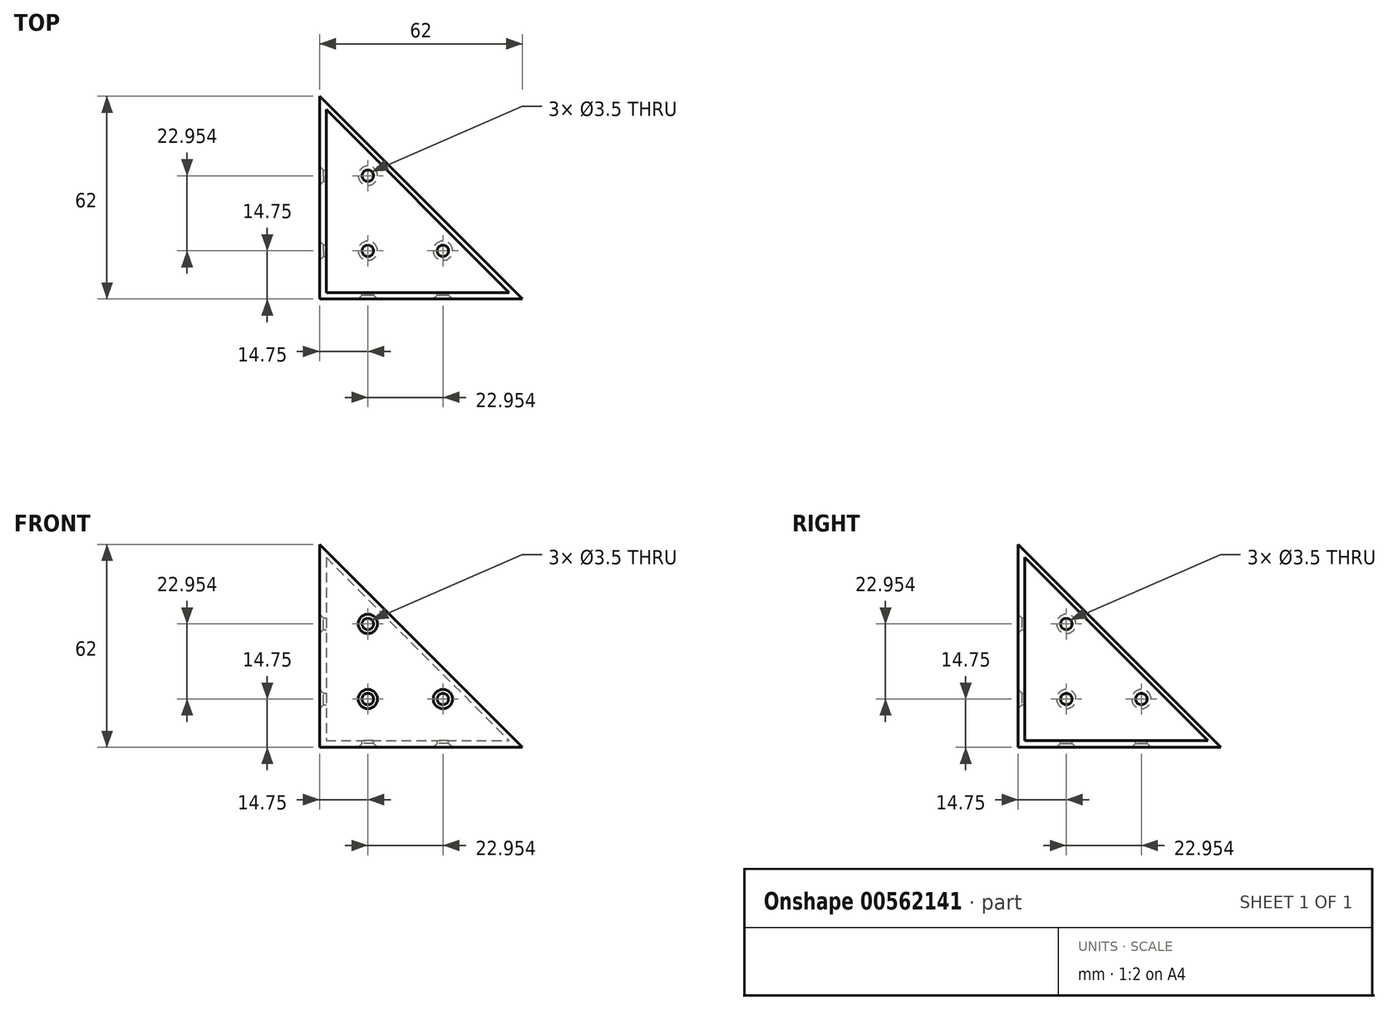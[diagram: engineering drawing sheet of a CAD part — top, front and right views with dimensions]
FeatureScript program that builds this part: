
annotation { "Feature Type Name" : "Feature", "Feature Type Description" : "" }
export const myFeature = defineFeature(function(context is Context, id is Id, definition is map)
    precondition{}
    {
        {
            var Q0;
            Q0=qCreatedBy(makeId("Top.planeOp"),FACE);
            var sketch = newSketch(context, id + "F0", { "sketchPlane" : qUnion([Q0])});
            skLineSegment(sketch, "E0", {"start": v(31, 31) * mm, "end": v(0, 0) * mm});
            skLineSegment(sketch, "E1", {"start": v(0, 0) * mm, "end": v(62, 0) * mm});
            skLineSegment(sketch, "E2", {"start": v(62, 0) * mm, "end": v(31, 31) * mm});
            skSolve(sketch);
        }
        {
            var Q0;
            Q0 = qSketchRegion(id + "F0", true);
            extrude(context, id + "F1", {"entities" : qUnion([Q0]), "depth" : 2 * mm, "offsetDistance" : 25 * mm});
        }
        {
            var Q0;
            Q0=makeQuery(id+"F1.opExtrude","CAP_FACE",FACE,{"disambiguationData":[OSD([sQuery(id+"F0.wireOp",EDGE,"E0"),sQuery(id+"F0.wireOp",EDGE,"E1"),sQuery(id+"F0.wireOp",EDGE,"E2")])],"isStart":false});
            var sketch = newSketch(context, id + "F2", { "sketchPlane" : qUnion([Q0])});
            skLineSegment(sketch, "E3", {"start": v(0, 0) * mm, "end": v(62, 0) * mm});
            skLineSegment(sketch, "E4", {"start": v(62, 0) * mm, "end": v(60, 2) * mm});
            skLineSegment(sketch, "E5", {"start": v(60, 2) * mm, "end": v(2, 2) * mm});
            skLineSegment(sketch, "E6", {"start": v(2, 2) * mm, "end": v(0, 0) * mm});
            skSolve(sketch);
        }
        {
            var Q0;
            Q0=makeQuery(id+"F2.imprint","IMPRINT",FACE,{"disambiguationData":[TD([[makeQuery(id+"F2.imprint","IMPRINT",EDGE,{"derivedFrom":sQuery(id+"F2.wireOp",EDGE,"E3")}),1.0]])]});
            extrude(context, id + "F3", {"entities" : qUnion([Q0]), "operationType" : NewBodyOperationType.ADD, "depth" : 60 * mm, "offsetDistance" : 25 * mm});
        }
        {
            var Q0;
            Q0=makeQuery(id+"F3.boolean.opBoolean","MERGE",FACE,{"derivedFrom":[makeQuery(id+"F1.opExtrude","SWEPT_FACE",FACE,{"disambiguationData":[OSD([sQuery(id+"F0.wireOp",EDGE,"E1")])]}),makeQuery(id+"F3.opExtrude","SWEPT_FACE",FACE,{"disambiguationData":[OSD([sQuery(id+"F2.wireOp",EDGE,"E3")])]})]});
            var sketch = newSketch(context, id + "F4", { "sketchPlane" : qUnion([Q0])});
            skLineSegment(sketch, "E7", {"start": v(0, 62) * mm, "end": v(62, 0) * mm});
            skSolve(sketch);
        }
        {
            var Q0;
            Q0=makeQuery(id+"F4.imprint","IMPRINT",FACE,{"disambiguationData":[TD([[makeQuery(id+"F4.imprint","IMPRINT",EDGE,{"derivedFrom":sQuery(id+"F4.wireOp",EDGE,"E7")}),1.0]])]});
            extrude(context, id + "F5", {"entities" : qUnion([Q0]), "operationType" : NewBodyOperationType.REMOVE, "endBound" : BoundingType.THROUGH_ALL, "oppositeDirection" : true, "depth" : 25 * mm, "offsetDistance" : 25 * mm});
        }
        {
            var Q0;
            Q0=makeQuery(id+"F3.opExtrude","SWEPT_FACE",FACE,{"disambiguationData":[OSD([sQuery(id+"F2.wireOp",EDGE,"E5")])]});
            var sketch = newSketch(context, id + "F6", { "sketchPlane" : qUnion([Q0])});
            skCircle(sketch, "E8", {"center": v(-14.75, 14.75) * mm, "radius": 1.75 * mm});
            skCircle(sketch, "E9", {"center": v(-14.75, 37.7) * mm, "radius": 1.75 * mm});
            skCircle(sketch, "E10", {"center": v(-37.7, 14.75) * mm, "radius": 1.75 * mm});
            skSolve(sketch);
        }
        {
            var Q0;
            Q0 = qSketchRegion(id + "F6", true);
            extrude(context, id + "F7", {"entities" : qUnion([Q0]), "operationType" : NewBodyOperationType.REMOVE, "endBound" : BoundingType.THROUGH_ALL, "oppositeDirection" : true, "depth" : 25 * mm, "offsetDistance" : 25 * mm});
        }
        {
            var Q0;
            Q0=makeQuery(id+"F1.opExtrude","SWEPT_BODY",BODY,{"disambiguationData":[OSD([sQuery(id+"F0.wireOp",EDGE,"E0"),sQuery(id+"F0.wireOp",EDGE,"E1"),sQuery(id+"F0.wireOp",EDGE,"E2")])]});
            var Q1;
            Q1=makeQuery(id+"F3.boolean.opBoolean","MERGE",FACE,{"derivedFrom":[makeQuery(id+"F1.opExtrude","SWEPT_FACE",FACE,{"disambiguationData":[OSD([sQuery(id+"F0.wireOp",EDGE,"E0")])]}),makeQuery(id+"F3.opExtrude","SWEPT_FACE",FACE,{"disambiguationData":[OSD([sQuery(id+"F2.wireOp",EDGE,"E6")])]})]});
            mirror(context, id + "F8", {"operationType" : NewBodyOperationType.ADD, "entities" : qUnion([Q0]), "mirrorPlane" : qUnion([Q1])});
        }
        {
            var Q0;
            {var subQ0=makeQuery(id+"F1.opExtrude","CAP_FACE",FACE,{"disambiguationData":[OSD([sQuery(id+"F0.wireOp",EDGE,"E0"),sQuery(id+"F0.wireOp",EDGE,"E1"),sQuery(id+"F0.wireOp",EDGE,"E2")])],"isStart":false});Q0=makeQuery(id+"F8.boolean.opBoolean","MERGE",FACE,{"derivedFrom":[subQ0,makeQuery(id+"F8.opPattern","COPY",FACE,{"derivedFrom":subQ0,"instanceName":"1"})]});}
            var sketch = newSketch(context, id + "F9", { "sketchPlane" : qUnion([Q0])});
            skCircle(sketch, "E11", {"center": v(14.75, 14.75) * mm, "radius": 1.75 * mm});
            skCircle(sketch, "E12", {"center": v(37.7, 14.75) * mm, "radius": 1.75 * mm});
            skCircle(sketch, "E13", {"center": v(14.75, 37.7) * mm, "radius": 1.75 * mm});
            skSolve(sketch);
        }
        {
            var Q0;
            Q0 = qSketchRegion(id + "F9", true);
            extrude(context, id + "F10", {"entities" : qUnion([Q0]), "operationType" : NewBodyOperationType.REMOVE, "endBound" : BoundingType.THROUGH_ALL, "oppositeDirection" : true, "depth" : 25 * mm, "offsetDistance" : 25 * mm});
        }
        {
            var Q0;
            {var subQ0=sQuery(id+"F0.wireOp",EDGE,"E2");var subQ1=sQuery(id+"F0.wireOp",EDGE,"E1");Q0=makeQuery(id+"F5.boolean.opBoolean","MERGE",VERTEX,{"derivedFrom":[makeQuery(id+"F1.opExtrude","CAP_VERTEX",VERTEX,{"disambiguationData":[OSD([subQ1,subQ0])],"isStart":true}),makeQuery(id+"F5.opExtrude","CAP_VERTEX",VERTEX,{"disambiguationData":[OSD([subQ1,subQ0,sQuery(id+"F2.wireOp",EDGE,"E3"),sQuery(id+"F2.wireOp",EDGE,"E4"),sQuery(id+"F4.wireOp",EDGE,"E7")])],"isStart":true})]});}
            var Q1;
            {var subQ0=sQuery(id+"F0.wireOp",EDGE,"E2");var subQ1=sQuery(id+"F0.wireOp",EDGE,"E1");Q1=makeQuery(id+"F8.opPattern","COPY",VERTEX,{"derivedFrom":makeQuery(id+"F5.boolean.opBoolean","MERGE",VERTEX,{"derivedFrom":[makeQuery(id+"F1.opExtrude","CAP_VERTEX",VERTEX,{"disambiguationData":[OSD([subQ1,subQ0])],"isStart":true}),makeQuery(id+"F5.opExtrude","CAP_VERTEX",VERTEX,{"disambiguationData":[OSD([subQ1,subQ0,sQuery(id+"F2.wireOp",EDGE,"E3"),sQuery(id+"F2.wireOp",EDGE,"E4"),sQuery(id+"F4.wireOp",EDGE,"E7")])],"isStart":true})]}),"instanceName":"1"});}
            var Q2;
            {var subQ0=sQuery(id+"F2.wireOp",EDGE,"E6");var subQ1=sQuery(id+"F2.wireOp",EDGE,"E3");var subQ2=makeQuery(id+"F5.boolean.opBoolean","MERGE",VERTEX,{"derivedFrom":[makeQuery(id+"F3.opExtrude","CAP_VERTEX",VERTEX,{"disambiguationData":[OSD([subQ1,subQ0])],"isStart":false}),makeQuery(id+"F5.opExtrude","CAP_VERTEX",VERTEX,{"disambiguationData":[OSD([sQuery(id+"F0.wireOp",EDGE,"E0"),sQuery(id+"F0.wireOp",EDGE,"E1"),subQ1,subQ0,sQuery(id+"F4.wireOp",EDGE,"E7")])],"isStart":true})]});Q2=makeQuery(id+"F8.boolean.opBoolean","MERGE",VERTEX,{"derivedFrom":[subQ2,makeQuery(id+"F8.opPattern","COPY",VERTEX,{"derivedFrom":subQ2,"instanceName":"1"})]});}
            cPlane(context, id + "F11", {"entities" : qUnion([Q0, Q1, Q2]), "cplaneType" : CPlaneType.THREE_POINT, "offset" : 25 * mm, "width" : 150 * mm, "height" : 150 * mm});
        }
        {
            var Q0;
            Q0=qCreatedBy(id+"F11.planeOp",FACE);
            var sketch = newSketch(context, id + "F12", { "sketchPlane" : qUnion([Q0])});
            skPoint(sketch, "E14.0", {"position": v(-25.31, 43.84) * mm});
            skPoint(sketch, "E14.1", {"position": v(50.62, 0) * mm});
            skPoint(sketch, "E14.2", {"position": v(-25.31, -43.84) * mm});
            skLineSegment(sketch, "E15", {"start": v(50.62, 0) * mm, "end": v(-25.31, 43.84) * mm});
            skLineSegment(sketch, "E16", {"start": v(-25.31, -43.84) * mm, "end": v(50.62, 0) * mm});
            skLineSegment(sketch, "E17", {"start": v(-25.31, -43.84) * mm, "end": v(-25.31, 43.84) * mm});
            skSolve(sketch);
        }
        {
            var Q0;
            Q0 = qSketchRegion(id + "F12", true);
            extrude(context, id + "F13", {"entities" : qUnion([Q0]), "operationType" : NewBodyOperationType.REMOVE, "endBound" : BoundingType.THROUGH_ALL, "oppositeDirection" : true, "depth" : 25 * mm, "offsetDistance" : 25 * mm});
        }
        {
            var Q0;
            {var subQ0=makeQuery(id+"F1.opExtrude","CAP_FACE",FACE,{"disambiguationData":[OSD([sQuery(id+"F0.wireOp",EDGE,"E0"),sQuery(id+"F0.wireOp",EDGE,"E1"),sQuery(id+"F0.wireOp",EDGE,"E2")])],"isStart":true});Q0=makeQuery(id+"F10.boolean.opBoolean","INTERSECT",EDGE,{"derivedFrom":[makeQuery(id+"F8.boolean.opBoolean","MERGE",FACE,{"derivedFrom":[subQ0,makeQuery(id+"F8.opPattern","COPY",FACE,{"derivedFrom":subQ0,"instanceName":"1"})]}),makeQuery(id+"F10.opExtrude","SWEPT_FACE",FACE,{"disambiguationData":[OSD([sQuery(id+"F9.wireOp",EDGE,"E13")])]})]});}
            var Q1;
            {var subQ0=makeQuery(id+"F1.opExtrude","CAP_FACE",FACE,{"disambiguationData":[OSD([sQuery(id+"F0.wireOp",EDGE,"E0"),sQuery(id+"F0.wireOp",EDGE,"E1"),sQuery(id+"F0.wireOp",EDGE,"E2")])],"isStart":true});Q1=makeQuery(id+"F10.boolean.opBoolean","INTERSECT",EDGE,{"derivedFrom":[makeQuery(id+"F8.boolean.opBoolean","MERGE",FACE,{"derivedFrom":[subQ0,makeQuery(id+"F8.opPattern","COPY",FACE,{"derivedFrom":subQ0,"instanceName":"1"})]}),makeQuery(id+"F10.opExtrude","SWEPT_FACE",FACE,{"disambiguationData":[OSD([sQuery(id+"F9.wireOp",EDGE,"E11")])]})]});}
            var Q2;
            {var subQ0=makeQuery(id+"F1.opExtrude","CAP_FACE",FACE,{"disambiguationData":[OSD([sQuery(id+"F0.wireOp",EDGE,"E0"),sQuery(id+"F0.wireOp",EDGE,"E1"),sQuery(id+"F0.wireOp",EDGE,"E2")])],"isStart":true});Q2=makeQuery(id+"F10.boolean.opBoolean","INTERSECT",EDGE,{"derivedFrom":[makeQuery(id+"F8.boolean.opBoolean","MERGE",FACE,{"derivedFrom":[subQ0,makeQuery(id+"F8.opPattern","COPY",FACE,{"derivedFrom":subQ0,"instanceName":"1"})]}),makeQuery(id+"F10.opExtrude","SWEPT_FACE",FACE,{"disambiguationData":[OSD([sQuery(id+"F9.wireOp",EDGE,"E12")])]})]});}
            var Q3;
            Q3=makeQuery(id+"F8.opPattern","COPY",EDGE,{"derivedFrom":makeQuery(id+"F7.boolean.opBoolean","INTERSECT",EDGE,{"derivedFrom":[makeQuery(id+"F3.boolean.opBoolean","MERGE",FACE,{"derivedFrom":[makeQuery(id+"F1.opExtrude","SWEPT_FACE",FACE,{"disambiguationData":[OSD([sQuery(id+"F0.wireOp",EDGE,"E1")])]}),makeQuery(id+"F3.opExtrude","SWEPT_FACE",FACE,{"disambiguationData":[OSD([sQuery(id+"F2.wireOp",EDGE,"E3")])]})]}),makeQuery(id+"F7.opExtrude","SWEPT_FACE",FACE,{"disambiguationData":[OSD([sQuery(id+"F6.wireOp",EDGE,"E8")])]})]}),"instanceName":"1"});
            var Q4;
            Q4=makeQuery(id+"F8.opPattern","COPY",EDGE,{"derivedFrom":makeQuery(id+"F7.boolean.opBoolean","INTERSECT",EDGE,{"derivedFrom":[makeQuery(id+"F3.boolean.opBoolean","MERGE",FACE,{"derivedFrom":[makeQuery(id+"F1.opExtrude","SWEPT_FACE",FACE,{"disambiguationData":[OSD([sQuery(id+"F0.wireOp",EDGE,"E1")])]}),makeQuery(id+"F3.opExtrude","SWEPT_FACE",FACE,{"disambiguationData":[OSD([sQuery(id+"F2.wireOp",EDGE,"E3")])]})]}),makeQuery(id+"F7.opExtrude","SWEPT_FACE",FACE,{"disambiguationData":[OSD([sQuery(id+"F6.wireOp",EDGE,"E10")])]})]}),"instanceName":"1"});
            var Q5;
            Q5=makeQuery(id+"F8.opPattern","COPY",EDGE,{"derivedFrom":makeQuery(id+"F7.boolean.opBoolean","INTERSECT",EDGE,{"derivedFrom":[makeQuery(id+"F3.boolean.opBoolean","MERGE",FACE,{"derivedFrom":[makeQuery(id+"F1.opExtrude","SWEPT_FACE",FACE,{"disambiguationData":[OSD([sQuery(id+"F0.wireOp",EDGE,"E1")])]}),makeQuery(id+"F3.opExtrude","SWEPT_FACE",FACE,{"disambiguationData":[OSD([sQuery(id+"F2.wireOp",EDGE,"E3")])]})]}),makeQuery(id+"F7.opExtrude","SWEPT_FACE",FACE,{"disambiguationData":[OSD([sQuery(id+"F6.wireOp",EDGE,"E9")])]})]}),"instanceName":"1"});
            var Q6;
            Q6=makeQuery(id+"F7.boolean.opBoolean","INTERSECT",EDGE,{"derivedFrom":[makeQuery(id+"F3.boolean.opBoolean","MERGE",FACE,{"derivedFrom":[makeQuery(id+"F1.opExtrude","SWEPT_FACE",FACE,{"disambiguationData":[OSD([sQuery(id+"F0.wireOp",EDGE,"E1")])]}),makeQuery(id+"F3.opExtrude","SWEPT_FACE",FACE,{"disambiguationData":[OSD([sQuery(id+"F2.wireOp",EDGE,"E3")])]})]}),makeQuery(id+"F7.opExtrude","SWEPT_FACE",FACE,{"disambiguationData":[OSD([sQuery(id+"F6.wireOp",EDGE,"E9")])]})]});
            var Q7;
            Q7=makeQuery(id+"F7.boolean.opBoolean","INTERSECT",EDGE,{"derivedFrom":[makeQuery(id+"F3.boolean.opBoolean","MERGE",FACE,{"derivedFrom":[makeQuery(id+"F1.opExtrude","SWEPT_FACE",FACE,{"disambiguationData":[OSD([sQuery(id+"F0.wireOp",EDGE,"E1")])]}),makeQuery(id+"F3.opExtrude","SWEPT_FACE",FACE,{"disambiguationData":[OSD([sQuery(id+"F2.wireOp",EDGE,"E3")])]})]}),makeQuery(id+"F7.opExtrude","SWEPT_FACE",FACE,{"disambiguationData":[OSD([sQuery(id+"F6.wireOp",EDGE,"E10")])]})]});
            var Q8;
            Q8=makeQuery(id+"F7.boolean.opBoolean","INTERSECT",EDGE,{"derivedFrom":[makeQuery(id+"F3.boolean.opBoolean","MERGE",FACE,{"derivedFrom":[makeQuery(id+"F1.opExtrude","SWEPT_FACE",FACE,{"disambiguationData":[OSD([sQuery(id+"F0.wireOp",EDGE,"E1")])]}),makeQuery(id+"F3.opExtrude","SWEPT_FACE",FACE,{"disambiguationData":[OSD([sQuery(id+"F2.wireOp",EDGE,"E3")])]})]}),makeQuery(id+"F7.opExtrude","SWEPT_FACE",FACE,{"disambiguationData":[OSD([sQuery(id+"F6.wireOp",EDGE,"E8")])]})]});
            chamfer(context, id + "F14", {"entities" : qUnion([Q0, Q1, Q2, Q3, Q4, Q5, Q6, Q7, Q8]), "width" : 1.2 * mm, "tangentPropagation" : true});
        }
    });
